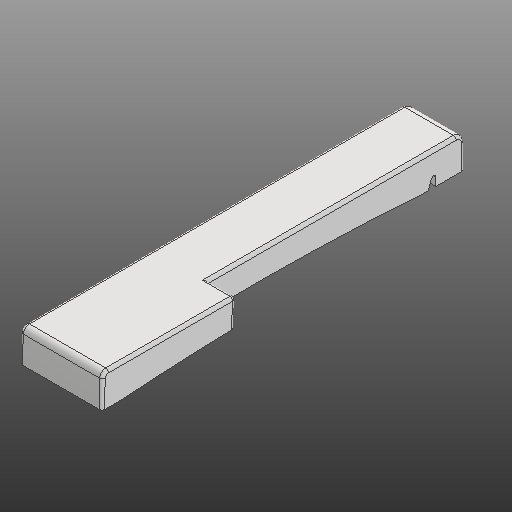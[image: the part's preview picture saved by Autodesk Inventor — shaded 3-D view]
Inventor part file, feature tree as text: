
AUTODESK INVENTOR PART (.ipt)
format: ipt  version: 2020 (Build 240168000, 168)  size: 308,224 bytes
history: native  units: in
note: dims shown in document units (in); Inventor stores cm internally (conversion verified against a paired STEP export)
features: extrude x4, other x3, fillet x2
ambient origin geometry x8: Origin, YZ Plane, XZ Plane, XY Plane, X Axis, Y Axis, Z Axis, Center Point
bodies: Solid1 (feature_tree)
feature tree (9):
  other  "Slot Start Plane"
  other  "Key Profile"
  extrude  "Upper (u)"  TaperAngle=0.0deg  [1 undecoded]
  extrude  "Lower (d)"  TaperAngle=0.0deg  [1 undecoded]
  extrude  "Protrusion Cutout"  Depth=0.0591in
  fillet  "Front Fillet"  Radius=0.1374in
  extrude  "Slot"  [1 undecoded]
  fillet  "Edge Softening"  Radius=0.0787in
  other  "Slot Sketch"
note: 3 required parameter values undecoded (feature->parameter linkage not recoverable at this tier; creation-order binding heuristic only, values carry confidence <= 0.55)
